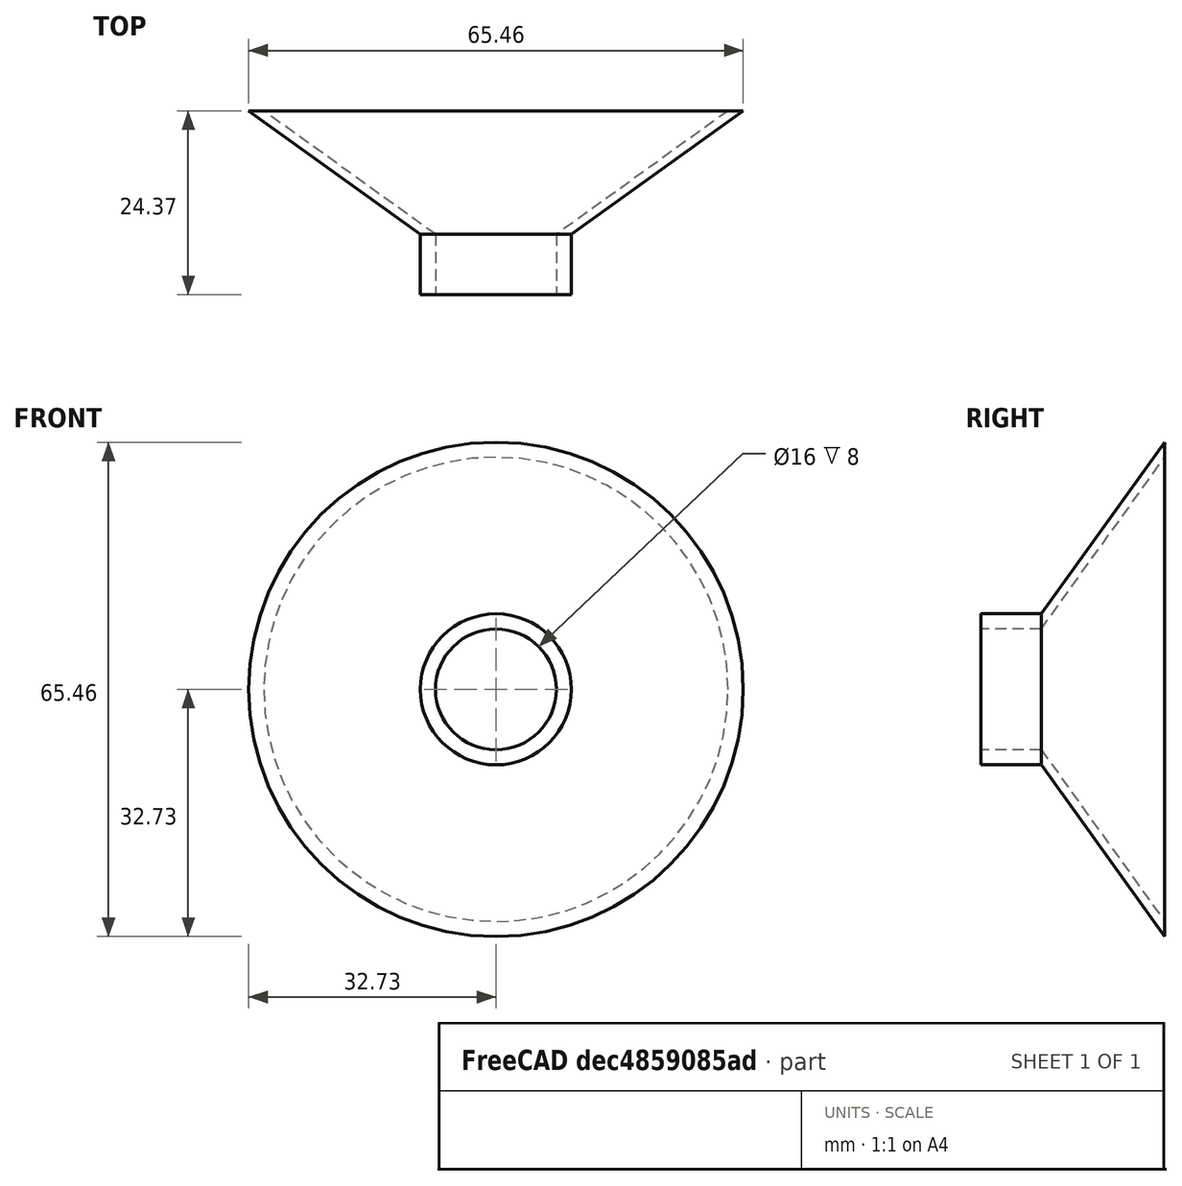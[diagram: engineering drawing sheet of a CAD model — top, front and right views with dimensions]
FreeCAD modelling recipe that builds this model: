
FCSTD DOCUMENT  (FreeCAD 0.22R38261 (Git))
Label: воронка
License: All rights reserved
LicenseURL: https://en.wikipedia.org/wiki/All_rights_reserved
objects: Sketcher::SketchObject×1, PartDesign::Revolution×1, PartDesign::Body×1
note: 5 computed .brp shape members not serialized (recipe doc carries the construction recipe); baked Part::Feature solids carry a one-line shape summary decoded from their .brp

FEATURE [Sketcher::SketchObject] Sketch
  AttachmentSupport = -> [XY_Plane]
  FullyConstrained = false
  MapMode = 5
  sketch-geometry (6):
    g0: LineSegment StartX=10 StartY=0 StartZ=0 EndX=12 EndY=0 EndZ=0
    g1: LineSegment StartX=12 StartY=0 StartZ=0 EndX=12 EndY=8 EndZ=0
    g2: LineSegment StartX=12 StartY=8 StartZ=0 EndX=32.7278 EndY=24.3669 EndZ=0
    g3: LineSegment StartX=32.7278 StartY=24.3669 StartZ=0 EndX=30.7278 EndY=24.3669 EndZ=0
    g4: LineSegment StartX=30.7278 StartY=24.3669 StartZ=0 EndX=10 EndY=8 EndZ=0
    g5: LineSegment StartX=10 StartY=8 StartZ=0 EndX=10 EndY=0 EndZ=0
  constraints (15):
    c: Coincident(g1,g0)
    c: Vertical(g1)
    c: Coincident(g5,g4)
    c: Vertical(g5)
    c: Horizontal(g3)
    c: Coincident(g3,g4)
    c: Coincident(g2,g3)
    c: Coincident(g1,g2)
    c: Distance(g3) = 2
    c: Horizontal(g1,g4)
    c: Coincident(g0,g5)
    c: Distance(g5) = 8
    c: Horizontal(g0)
    c: Distance(g0) = 2
    c: Distance(g-1,g0) = 12
FEATURE [PartDesign::Revolution] Revolution
  Angle = 360
  Angle2 = 60
  Axis = (0,1,0)
  Base = (0,0,0)
  Profile = -> Sketch
  ReferenceAxis = -> Sketch [V_Axis]
  Reversed = true
  Suppressed = false
  Type = 0
FEATURE [PartDesign::Body] Body  label="Тело"
  AllowCompound = false
  Group = -> [Sketch,Revolution]
  Origin = -> Origin
  Tip = -> Revolution
